# Revit family: LB4A
name_source: partatom
category: Lighting Fixtures
revit_build: Autodesk Revit 2014 (Build: 20130308_1515(x64)
units: mm (PartAtom-declared; Revit-internal decimal feet)

## types (1)
- LB4A
    Apparent Load = 9 VA
    Color Filter = 16777215
    Default Elevation = 48"
    Description = 4in Fixed or Directional Downlight
    Dimming Lamp Color Temperature Shift = <None>
    Emit Shape Visible in Rendering = No
    Emit from Circle Diameter = 3 3/4"
    Glass = Hubbell-White Glass
    Input Wattage = 9 W
    Lamp = LED
    Load Classification = Lighting
    Manufacturer = Prescolite
    Model = LB4A
    Photometric Web File = LB4A6L30K9_WH.ies
    Power Factor = 1
    Product Documentation Link = https://hubbellcdn.com
    Product Page URL = https://www.hubbell.com
    Tilt Angle = -90.00°
    Trim = Hubbell-White
    URL = https://www.hubbell.com
    Voltage = 120 V
    Warranty = 5 Year Warranty
    Wattage Comments = Energy saving LED light engine with 9-watt input power

## geometry (parser evidence)
native form markers: Blend x6, Sweep x1
no freeform markers — native parametric forms only
